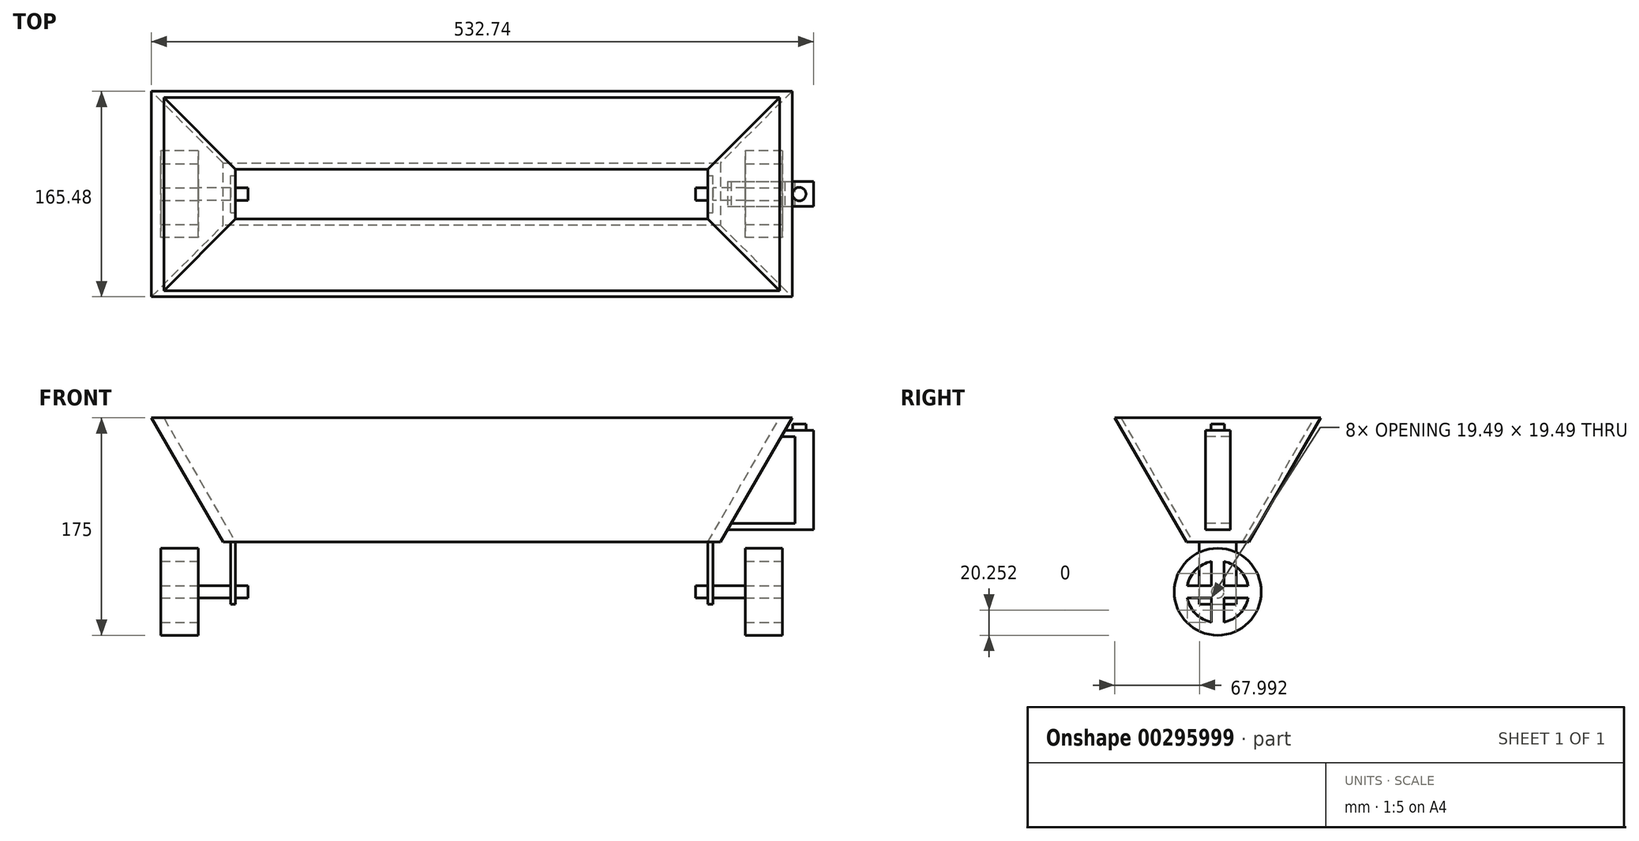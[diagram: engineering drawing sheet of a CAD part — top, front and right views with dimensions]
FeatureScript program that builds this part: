
annotation { "Feature Type Name" : "Feature", "Feature Type Description" : "" }
export const myFeature = defineFeature(function(context is Context, id is Id, definition is map)
    precondition{}
    {
        {
            var Q0;
            Q0=qCreatedBy(makeId("Top.planeOp"),FACE);
            var sketch = newSketch(context, id + "F0", { "sketchPlane" : qUnion([Q0])});
            skLineSegment(sketch, "E0.bottom", {"start": v(-200, 25) * mm, "end": v(200, 25) * mm});
            skLineSegment(sketch, "E0.top", {"start": v(-200, -25) * mm, "end": v(200, -25) * mm});
            skLineSegment(sketch, "E0.left", {"start": v(-200, 25) * mm, "end": v(-200, -25) * mm});
            skLineSegment(sketch, "E0.right", {"start": v(200, 25) * mm, "end": v(200, -25) * mm});
            skSolve(sketch);
        }
        {
            var Q0;
            Q0 = qSketchRegion(id + "F0", true);
            extrude(context, id + "F1", {"entities" : qUnion([Q0]), "depth" : 100 * mm, "hasDraft" : true, "draftAngle" : 30 * degree});
        }
        {
            var Q0;
            Q0=qCreatedBy(makeId("Top.planeOp"),FACE);
            var sketch = newSketch(context, id + "F2", { "sketchPlane" : qUnion([Q0])});
            skLineSegment(sketch, "E1.bottom", {"start": v(-190, 20) * mm, "end": v(190, 20) * mm});
            skLineSegment(sketch, "E1.top", {"start": v(-190, -20) * mm, "end": v(190, -20) * mm});
            skLineSegment(sketch, "E1.left", {"start": v(-190, 20) * mm, "end": v(-190, -20) * mm});
            skLineSegment(sketch, "E1.right", {"start": v(190, 20) * mm, "end": v(190, -20) * mm});
            skPoint(sketch, "E1.middle", {"position": v(0, 0) * mm});
            skSolve(sketch);
        }
        {
            var Q0;
            Q0 = qSketchRegion(id + "F2", true);
            extrude(context, id + "F3", {"entities" : qUnion([Q0]), "operationType" : NewBodyOperationType.REMOVE, "endBound" : BoundingType.UP_TO_NEXT, "depth" : 25 * mm, "hasDraft" : true, "draftAngle" : 30 * degree});
        }
        {
            var Q0;
            Q0=qCreatedBy(makeId("Right.planeOp"),FACE);
            cPlane(context, id + "F4", {"entities" : qUnion([Q0]), "cplaneType" : CPlaneType.OFFSET, "offset" : 260 * mm, "width" : 150 * mm, "height" : 150 * mm});
        }
        {
            var Q0;
            Q0=qCreatedBy(id+"F4.planeOp",FACE);
            var sketch = newSketch(context, id + "F5", { "sketchPlane" : qUnion([Q0])});
            skLineSegment(sketch, "E2.bottom", {"start": v(-10, 90) * mm, "end": v(10, 90) * mm});
            skLineSegment(sketch, "E2.top", {"start": v(-10, 10) * mm, "end": v(10, 10) * mm});
            skLineSegment(sketch, "E2.left", {"start": v(-10, 90) * mm, "end": v(-10, 10) * mm});
            skLineSegment(sketch, "E2.right", {"start": v(10, 90) * mm, "end": v(10, 10) * mm});
            skPoint(sketch, "E2.middle", {"position": v(0, 50) * mm});
            skSolve(sketch);
        }
        {
            var Q0;
            Q0 = qSketchRegion(id + "F5", true);
            extrude(context, id + "F6", {"entities" : qUnion([Q0]), "operationType" : NewBodyOperationType.ADD, "endBound" : BoundingType.UP_TO_NEXT, "oppositeDirection" : true, "depth" : 25 * mm, "hasSecondDirection" : true, "secondDirectionOppositeDirection" : false, "secondDirectionDepth" : 15 * mm});
        }
        {
            var Q0;
            Q0=qCreatedBy(id+"F4.planeOp",FACE);
            var sketch = newSketch(context, id + "F7", { "sketchPlane" : qUnion([Q0])});
            skLineSegment(sketch, "E3.bottom", {"start": v(-15, 85) * mm, "end": v(15, 85) * mm});
            skLineSegment(sketch, "E3.top", {"start": v(-15, 15) * mm, "end": v(15, 15) * mm});
            skLineSegment(sketch, "E3.left", {"start": v(-15, 85) * mm, "end": v(-15, 15) * mm});
            skLineSegment(sketch, "E3.right", {"start": v(15, 85) * mm, "end": v(15, 15) * mm});
            skPoint(sketch, "E3.middle", {"position": v(0, 50) * mm});
            skSolve(sketch);
        }
        {
            var Q0;
            Q0 = qSketchRegion(id + "F7", true);
            var Q1;
            Q1=makeQuery(id+"F1.opExtrude","SWEPT_FACE",FACE,{"disambiguationData":[OSD([sQuery(id+"F0.wireOp",EDGE,"E0.right")])]});
            var Q2;
            Q2=makeQuery(id+"F1.opExtrude","SWEPT_BODY",BODY,{"disambiguationData":[OSD([sQuery(id+"F0.wireOp",EDGE,"E0.bottom"),sQuery(id+"F0.wireOp",EDGE,"E0.top"),sQuery(id+"F0.wireOp",EDGE,"E0.left"),sQuery(id+"F0.wireOp",EDGE,"E0.right")])]});
            extrude(context, id + "F8", {"entities" : qUnion([Q0]), "operationType" : NewBodyOperationType.REMOVE, "endBound" : BoundingType.UP_TO_SURFACE, "oppositeDirection" : true, "endBoundEntityFace" : qUnion([Q1]), "endBoundEntityBody" : qUnion([Q2]), "depth" : 25 * mm});
        }
        {
            var Q0;
            Q0=makeQuery(id+"F6.opExtrude","SWEPT_FACE",FACE,{"disambiguationData":[OSD([sQuery(id+"F5.wireOp",EDGE,"E2.bottom")])]});
            var sketch = newSketch(context, id + "F9", { "sketchPlane" : qUnion([Q0])});
            skCircle(sketch, "E4", {"center": v(263.48, 0) * mm, "radius": 5.44 * mm});
            skPoint(sketch, "E4.centerSnap0", {"position": v(263.48, -10) * mm});
            skPoint(sketch, "E4.centerSnap1", {"position": v(251.96, 0) * mm});
            skSolve(sketch);
        }
        {
            var Q0;
            Q0 = qSketchRegion(id + "F9", true);
            extrude(context, id + "F10", {"entities" : qUnion([Q0]), "depth" : 5 * mm});
        }
        {
            var Q0;
            Q0=qCreatedBy(makeId("Right.planeOp"),FACE);
            var sketch = newSketch(context, id + "F11", { "sketchPlane" : qUnion([Q0])});
            skCircle(sketch, "E5", {"center": v(0, -40) * mm, "radius": 35 * mm});
            skSolve(sketch);
        }
        {
            var Q0;
            Q0=makeQuery(id+"F11.imprint","IMPRINT",FACE,{"disambiguationData":[TD([[makeQuery(id+"F11.imprint","IMPRINT",EDGE,{"derivedFrom":sQuery(id+"F11.wireOp",EDGE,"E5")}),1.0]])]});
            extrude(context, id + "F12", {"entities" : qUnion([Q0]), "depth" : 250 * mm, "hasSecondDirection" : true, "secondDirectionOppositeDirection" : true, "secondDirectionDepth" : 250 * mm});
        }
        {
            var Q0;
            Q0=qCreatedBy(makeId("Right.planeOp"),FACE);
            var sketch = newSketch(context, id + "F13", { "sketchPlane" : qUnion([Q0])});
            skCircle(sketch, "E6", {"center": v(0, -40) * mm, "radius": 35 * mm});
            skSolve(sketch);
        }
        {
            var Q0;
            Q0 = qSketchRegion(id + "F13", true);
            extrude(context, id + "F14", {"entities" : qUnion([Q0]), "operationType" : NewBodyOperationType.REMOVE, "oppositeDirection" : true, "depth" : 220 * mm, "hasSecondDirection" : true, "secondDirectionOppositeDirection" : false, "secondDirectionDepth" : 220 * mm});
        }
        {
            var Q0;
            Q0=qCreatedBy(makeId("Right.planeOp"),FACE);
            var sketch = newSketch(context, id + "F15", { "sketchPlane" : qUnion([Q0])});
            skCircle(sketch, "E7", {"center": v(0, -40) * mm, "radius": 35 * mm});
            skCircle(sketch, "E8", {"center": v(0, -40) * mm, "radius": 25 * mm});
            skLineSegment(sketch, "E9.bottom", {"start": v(-5, -15.5) * mm, "end": v(5, -15.5) * mm});
            skLineSegment(sketch, "E9.top", {"start": v(-5, -64.5) * mm, "end": v(5, -64.5) * mm});
            skLineSegment(sketch, "E9.left", {"start": v(-5, -15.5) * mm, "end": v(-5, -64.5) * mm});
            skLineSegment(sketch, "E9.right", {"start": v(5, -15.5) * mm, "end": v(5, -64.5) * mm});
            skLineSegment(sketch, "E10.bottom", {"start": v(-24.5, -45) * mm, "end": v(24.5, -45) * mm});
            skLineSegment(sketch, "E10.top", {"start": v(-24.5, -35) * mm, "end": v(24.5, -35) * mm});
            skLineSegment(sketch, "E10.left", {"start": v(-24.5, -45) * mm, "end": v(-24.5, -35) * mm});
            skLineSegment(sketch, "E10.right", {"start": v(24.5, -45) * mm, "end": v(24.5, -35) * mm});
            skSolve(sketch);
        }
        {
            var Q0;
            {var subQ0=sQuery(id+"F15.wireOp",EDGE,"E9.left");var subQ3=sQuery(id+"F15.wireOp",EDGE,"E10.top");var subQ5=makeQuery(id+"F15.imprint","INTERSECT",VERTEX,{"derivedFrom":[subQ0,subQ3]});Q0=makeQuery(id+"F15.imprint","IMPRINT",FACE,{"disambiguationData":[TD([[makeQuery(id+"F15.imprint","IMPRINT",EDGE,{"disambiguationData":[TD([[subQ5,1.0]])],"derivedFrom":subQ0}),-1.0]])]});}
            var Q1;
            {var subQ0=sQuery(id+"F15.wireOp",EDGE,"E9.left");var subQ3=sQuery(id+"F15.wireOp",EDGE,"E10.bottom");var subQ5=makeQuery(id+"F15.imprint","INTERSECT",VERTEX,{"derivedFrom":[subQ0,subQ3]});Q1=makeQuery(id+"F15.imprint","IMPRINT",FACE,{"disambiguationData":[TD([[makeQuery(id+"F15.imprint","IMPRINT",EDGE,{"disambiguationData":[TD([[subQ5,-1.0]])],"derivedFrom":subQ0}),-1.0]])]});}
            var Q2;
            {var subQ0=sQuery(id+"F15.wireOp",EDGE,"E9.right");var subQ3=sQuery(id+"F15.wireOp",EDGE,"E10.top");var subQ5=makeQuery(id+"F15.imprint","INTERSECT",VERTEX,{"derivedFrom":[subQ0,subQ3]});Q2=makeQuery(id+"F15.imprint","IMPRINT",FACE,{"disambiguationData":[TD([[makeQuery(id+"F15.imprint","IMPRINT",EDGE,{"disambiguationData":[TD([[subQ5,1.0]])],"derivedFrom":subQ0}),1.0]])]});}
            var Q3;
            {var subQ0=sQuery(id+"F15.wireOp",EDGE,"E9.right");var subQ3=sQuery(id+"F15.wireOp",EDGE,"E10.bottom");var subQ5=makeQuery(id+"F15.imprint","INTERSECT",VERTEX,{"derivedFrom":[subQ0,subQ3]});Q3=makeQuery(id+"F15.imprint","IMPRINT",FACE,{"disambiguationData":[TD([[makeQuery(id+"F15.imprint","IMPRINT",EDGE,{"disambiguationData":[TD([[subQ5,-1.0]])],"derivedFrom":subQ0}),1.0]])]});}
            extrude(context, id + "F16", {"entities" : qUnion([Q0, Q1, Q2, Q3]), "operationType" : NewBodyOperationType.REMOVE, "endBound" : BoundingType.THROUGH_ALL, "oppositeDirection" : true, "depth" : 25 * mm, "hasSecondDirection" : true, "secondDirectionBound" : SecondDirectionBoundingType.THROUGH_ALL, "secondDirectionOppositeDirection" : false, "secondDirectionDepth" : 25 * mm});
        }
        {
            var Q0;
            Q0=qCreatedBy(makeId("Right.planeOp"),FACE);
            var sketch = newSketch(context, id + "F17", { "sketchPlane" : qUnion([Q0])});
            skCircle(sketch, "E11", {"center": v(0, -40) * mm, "radius": 5 * mm});
            skSolve(sketch);
        }
        {
            var Q0;
            Q0 = qSketchRegion(id + "F17", true);
            extrude(context, id + "F18", {"entities" : qUnion([Q0]), "operationType" : NewBodyOperationType.ADD, "endBound" : BoundingType.UP_TO_NEXT, "depth" : 25 * mm, "hasSecondDirection" : true, "secondDirectionBound" : SecondDirectionBoundingType.UP_TO_NEXT, "secondDirectionOppositeDirection" : true, "secondDirectionDepth" : 25 * mm});
        }
        {
            var Q0;
            Q0=qCreatedBy(makeId("Top.planeOp"),FACE);
            var sketch = newSketch(context, id + "F19", { "sketchPlane" : qUnion([Q0])});
            skLineSegment(sketch, "E12.bottom", {"start": v(190, -15) * mm, "end": v(194, -15) * mm});
            skLineSegment(sketch, "E12.top", {"start": v(190, 15) * mm, "end": v(194, 15) * mm});
            skLineSegment(sketch, "E12.left", {"start": v(190, -15) * mm, "end": v(190, 15) * mm});
            skLineSegment(sketch, "E12.right", {"start": v(194, -15) * mm, "end": v(194, 15) * mm});
            skPoint(sketch, "E12.middle", {"position": v(192, 0) * mm});
            skLineSegment(sketch, "E13.bottom", {"start": v(-194, -15) * mm, "end": v(-190, -15) * mm});
            skLineSegment(sketch, "E13.top", {"start": v(-194, 15) * mm, "end": v(-190, 15) * mm});
            skLineSegment(sketch, "E13.left", {"start": v(-194, -15) * mm, "end": v(-194, 15) * mm});
            skLineSegment(sketch, "E13.right", {"start": v(-190, -15) * mm, "end": v(-190, 15) * mm});
            skPoint(sketch, "E13.middle", {"position": v(-192, 0) * mm});
            skSolve(sketch);
        }
        {
            var Q0;
            Q0 = qSketchRegion(id + "F19", true);
            extrude(context, id + "F20", {"entities" : qUnion([Q0]), "operationType" : NewBodyOperationType.ADD, "oppositeDirection" : true, "depth" : 50 * mm});
        }
        {
            var Q0;
            Q0=qCreatedBy(makeId("Right.planeOp"),FACE);
            var sketch = newSketch(context, id + "F21", { "sketchPlane" : qUnion([Q0])});
            skCircle(sketch, "E14", {"center": v(0, -40) * mm, "radius": 25 * mm});
            skSolve(sketch);
        }
        {
            var Q0;
            Q0 = qSketchRegion(id + "F21", true);
            extrude(context, id + "F22", {"entities" : qUnion([Q0]), "operationType" : NewBodyOperationType.REMOVE, "oppositeDirection" : true, "depth" : 180 * mm, "hasSecondDirection" : true, "secondDirectionOppositeDirection" : false, "secondDirectionDepth" : 180 * mm});
        }
    });
